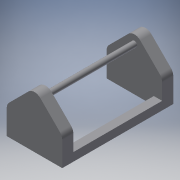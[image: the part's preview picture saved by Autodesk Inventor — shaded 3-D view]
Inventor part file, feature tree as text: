
AUTODESK INVENTOR PART (.ipt)
format: ipt  version: 2017 (Build 210142000, 142)  size: 142,848 bytes
history: native  units: mm
features: other x3, extrude x2, sketch x2, projected_geometry x2, chamfer x1, fillet x1, reference x1
ambient origin geometry x8: Origin, YZ Plane, XZ Plane, XY Plane, X Axis, Y Axis, Z Axis, Center Point
bodies: Solid1 (feature_tree)
feature tree (12):
  extrude  "Extrusion1"  Depth=200.0mm TaperAngle=0.0deg
  chamfer  "Chamfer1"  Distance=100.0mm Angle=45.0deg
  fillet  "Fillet1"  Radius=30.0mm
  extrude  "Extrusion2"  Depth=200.0mm TaperAngle=0.0deg
  sketch  "Sketch1"  dims[d0=200.0mm d1=200.0mm d2=0.0mm d3=100.0mm d4=2.0mm d5=45.0deg d6=30.0mm]
  reference  "Reference1"
  sketch  "Sketch2"  dims[d7=20.0mm d8=200.0mm d9=0.0mm d10=30.0mm d11=30.0mm]
  projected_geometry  "Projected Loop1"
  projected_geometry  "Projected Loop2"
  other  "<userpath>\OneDrive\Inventor\VolledigGeassembleerdv001.iam"
  other  "VolledigGeassembleerdv001.iam"
  other  "Frame:1"
